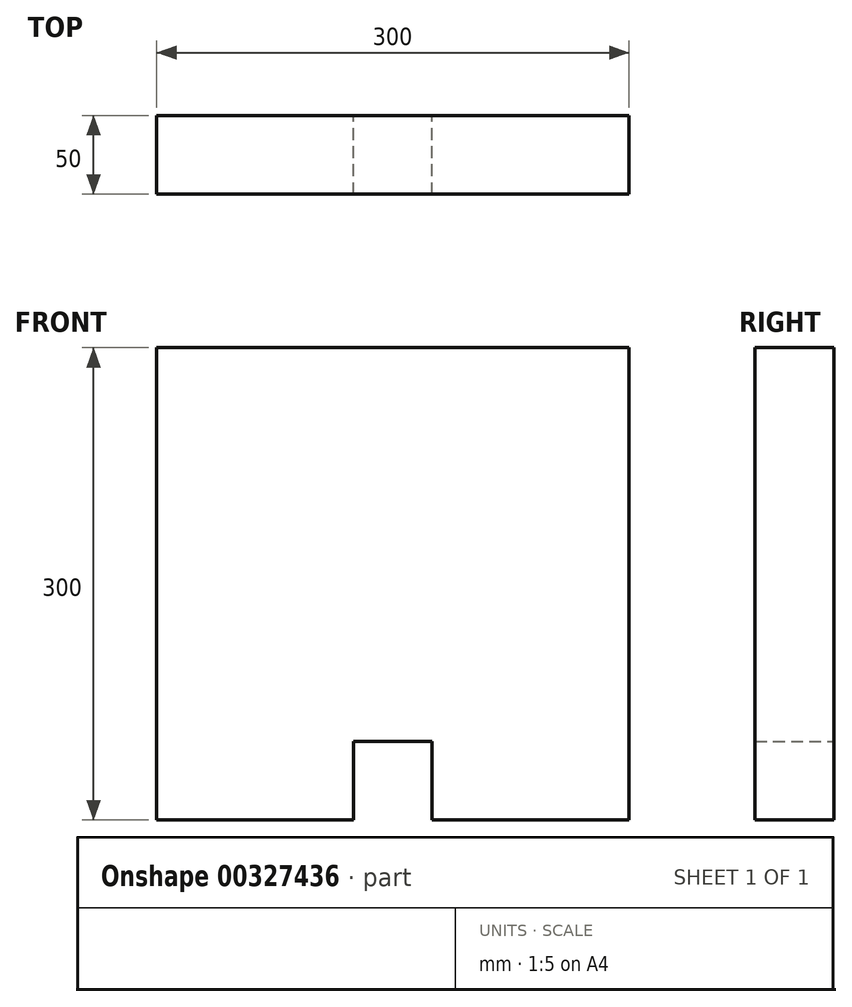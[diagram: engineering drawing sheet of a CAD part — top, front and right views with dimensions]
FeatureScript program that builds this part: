
annotation { "Feature Type Name" : "Feature", "Feature Type Description" : "" }
export const myFeature = defineFeature(function(context is Context, id is Id, definition is map)
    precondition{}
    {
        {
            var Q0;
            Q0=qCreatedBy(makeId("Front.planeOp"),FACE);
            var sketch = newSketch(context, id + "F0", { "sketchPlane" : qUnion([Q0])});
            skLineSegment(sketch, "E0", {"start": v(-228.78, -91.89) * mm, "end": v(-103.78, -91.89) * mm});
            skLineSegment(sketch, "E1", {"start": v(-103.78, -41.89) * mm, "end": v(-103.78, -91.89) * mm});
            skLineSegment(sketch, "E2", {"start": v(-53.78, -41.89) * mm, "end": v(-53.78, -91.89) * mm});
            skLineSegment(sketch, "E3", {"start": v(-103.78, -41.89) * mm, "end": v(-53.78, -41.89) * mm});
            skLineSegment(sketch, "E4.trimOffspring", {"start": v(-53.78, -91.89) * mm, "end": v(71.22, -91.89) * mm});
            skLineSegment(sketch, "E5", {"start": v(-228.78, -91.89) * mm, "end": v(-228.78, 208.11) * mm});
            skLineSegment(sketch, "E6", {"start": v(-228.78, 208.11) * mm, "end": v(71.22, 208.11) * mm});
            skLineSegment(sketch, "E7", {"start": v(71.22, 208.11) * mm, "end": v(71.22, -91.89) * mm});
            skSolve(sketch);
        }
        {
            var Q0;
            Q0 = qSketchRegion(id + "F0", true);
            extrude(context, id + "F1", {"entities" : qUnion([Q0]), "depth" : 50 * mm});
        }
    });
